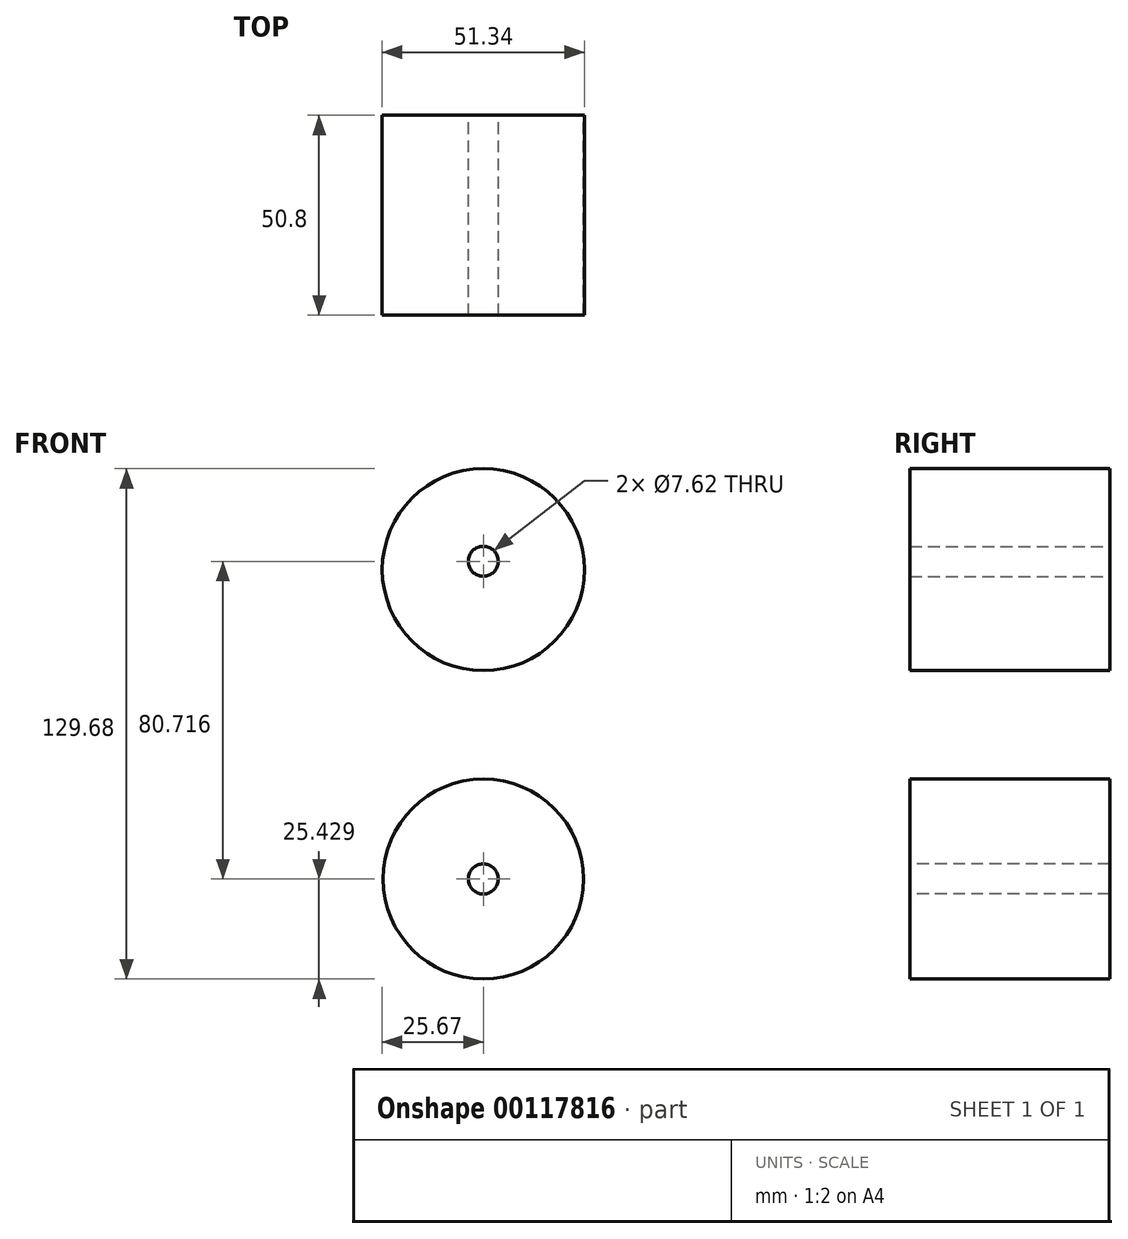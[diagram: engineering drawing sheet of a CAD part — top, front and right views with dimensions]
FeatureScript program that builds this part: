
annotation { "Feature Type Name" : "Feature", "Feature Type Description" : "" }
export const myFeature = defineFeature(function(context is Context, id is Id, definition is map)
    precondition{}
    {
        {
            var Q0;
            Q0=qCreatedBy(makeId("Front.planeOp"),FACE);
            var sketch = newSketch(context, id + "F0", { "sketchPlane" : qUnion([Q0])});
            skCircle(sketch, "E0", {"center": v(0, 47.44) * mm, "radius": 25.67 * mm});
            skCircle(sketch, "E1", {"center": v(0, -31.14) * mm, "radius": 25.43 * mm});
            skSolve(sketch);
        }
        {
            var Q0;
            Q0=makeQuery(id+"F0.imprint","IMPRINT",FACE,{"disambiguationData":[TD([[makeQuery(id+"F0.imprint","IMPRINT",EDGE,{"derivedFrom":sQuery(id+"F0.wireOp",EDGE,"E0")}),1.0]])]});
            var Q1;
            Q1=makeQuery(id+"F0.imprint","IMPRINT",FACE,{"disambiguationData":[TD([[makeQuery(id+"F0.imprint","IMPRINT",EDGE,{"derivedFrom":sQuery(id+"F0.wireOp",EDGE,"E1")}),1.0]])]});
            extrude(context, id + "F1", {"entities" : qUnion([Q0, Q1]), "depth" : 50.8 * mm});
        }
        {
            var Q0;
            Q0=qCreatedBy(makeId("Front.planeOp"),FACE);
            var sketch = newSketch(context, id + "F2", { "sketchPlane" : qUnion([Q0])});
            skCircle(sketch, "E2", {"center": v(0, 49.57) * mm, "radius": 3.12 * mm});
            skCircle(sketch, "E3", {"center": v(0, -31.07) * mm, "radius": 3.18 * mm});
            skSolve(sketch);
        }
        {
            var Q0;
            Q0=sQuery(id+"F2.wireOp",VERTEX,"E2.center");
            var Q1;
            Q1=makeQuery(id+"F1.opExtrude","SWEPT_BODY",BODY,{"disambiguationData":[OSD([sQuery(id+"F0.wireOp",EDGE,"E0")])]});
            hole(context, id + "F3", {"style" : HoleStyle.SIMPLE, "endStyle" : HoleEndStyle.THROUGH, "oppositeDirection" : true, "holeDiameter" : 7.62 * mm, "locations" : qUnion([Q0]), "scope" : qUnion([Q1]), "isTappedThrough" : true});
        }
        {
            var Q0;
            Q0=makeQuery(id+"F1.opExtrude","CAP_FACE",FACE,{"disambiguationData":[OSD([sQuery(id+"F0.wireOp",EDGE,"E1")])],"isStart":false});
            var sketch = newSketch(context, id + "F4", { "sketchPlane" : qUnion([Q0])});
            skCircle(sketch, "E4.0.0", {"center": v(0, -31.14) * mm, "radius": 25.43 * mm});
            skSolve(sketch);
        }
        {
            var Q0;
            Q0=sQuery(id+"F4.wireOp",VERTEX,"E4.0.0.center");
            var Q1;
            Q1=makeQuery(id+"F1.opExtrude","SWEPT_BODY",BODY,{"disambiguationData":[OSD([sQuery(id+"F0.wireOp",EDGE,"E1")])]});
            hole(context, id + "F5", {"style" : HoleStyle.SIMPLE, "endStyle" : HoleEndStyle.THROUGH, "holeDiameter" : 7.62 * mm, "locations" : qUnion([Q0]), "scope" : qUnion([Q1]), "isTappedThrough" : true});
        }
    });
